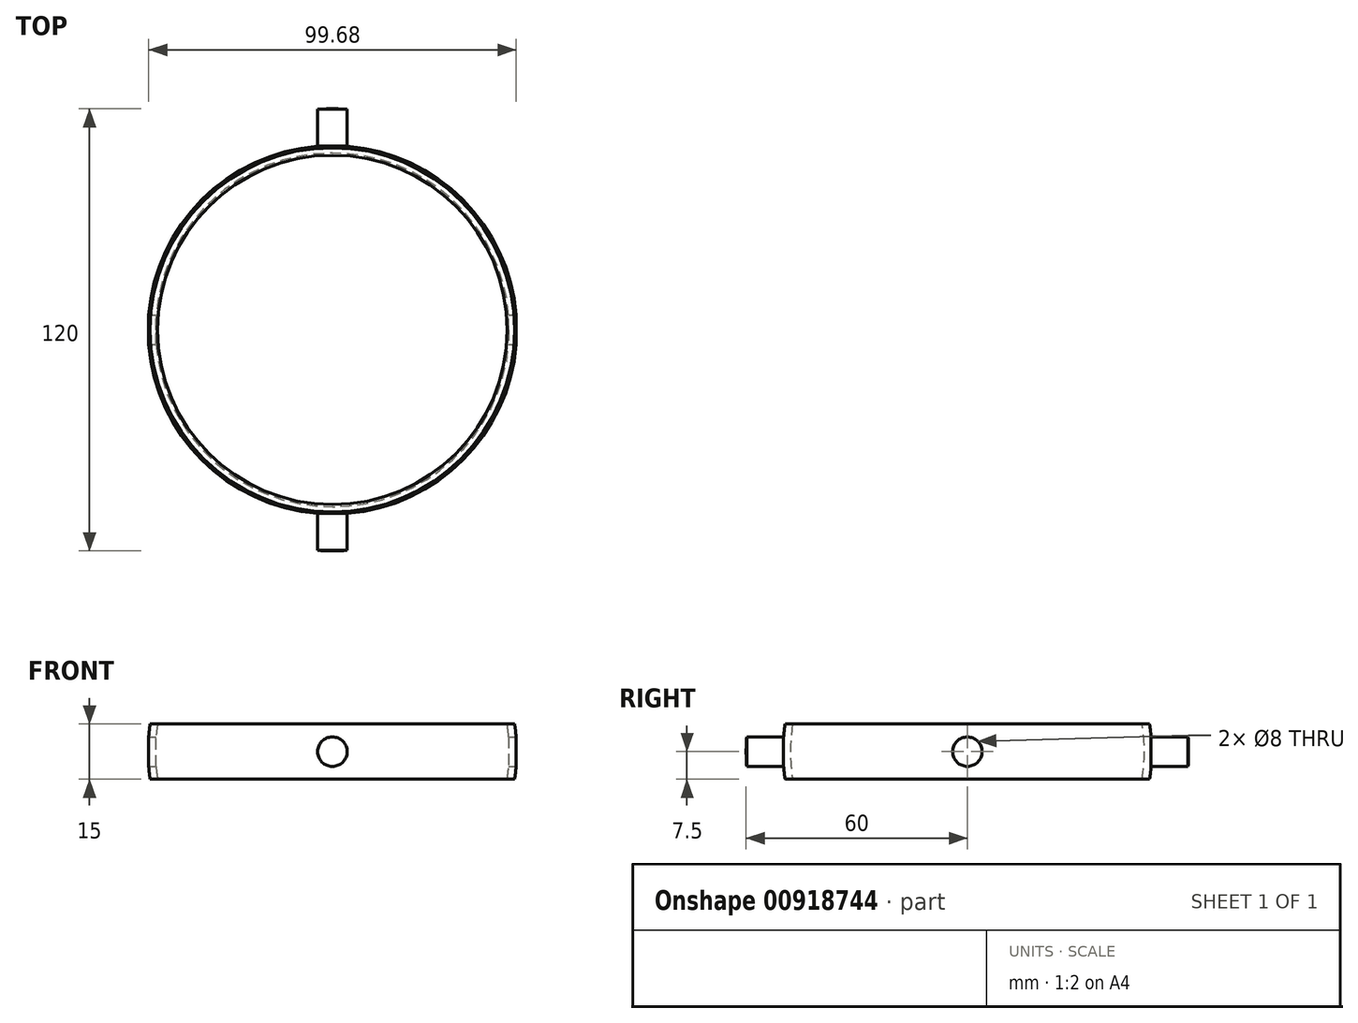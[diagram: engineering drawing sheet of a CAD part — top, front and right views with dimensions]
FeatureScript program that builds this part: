
annotation { "Feature Type Name" : "Feature", "Feature Type Description" : "" }
export const myFeature = defineFeature(function(context is Context, id is Id, definition is map)
    precondition{}
    {
        {
            var Q0;
            Q0=qCreatedBy(makeId("Front.planeOp"),FACE);
            var sketch = newSketch(context, id + "F0", { "sketchPlane" : qUnion([Q0])});
            skLineSegment(sketch, "E0", {"start": v(0, 15) * mm, "end": v(0, 0) * mm});
            skLineSegment(sketch, "E1", {"start": v(0, 0) * mm, "end": v(-54.5, 0) * mm});
            skArc(sketch, "E2", {"start": v(-49.43, 7.5) * mm, "mid": v(-50, 0) * mm, "end": v(-49.43, -7.5) * mm});
            skPoint(sketch, "E2.startSnap0", {"position": v(0, 7.5) * mm});
            skArc(sketch, "E3", {"start": v(-47.41, 7.5) * mm, "mid": v(-48, 0) * mm, "end": v(-47.41, -7.5) * mm});
            skLineSegment(sketch, "E4", {"start": v(-49.43, 7.5) * mm, "end": v(-47.41, 7.5) * mm});
            skLineSegment(sketch, "E5", {"start": v(-49.43, -7.5) * mm, "end": v(-47.41, -7.5) * mm});
            skSolve(sketch);
        }
        {
            var Q0;
            Q0 = qSketchRegion(id + "F0", true);
            var Q1;
            Q1=sQuery(id+"F0.wireOp",EDGE,"E0");
            revolve(context, id + "F1", {"surfaceOperationType" : NewSurfaceOperationType.NEW, "entities" : qUnion([Q0]), "axis" : qUnion([Q1]), "revolveType" : RevolveType.FULL});
        }
        {
            var Q0;
            Q0=qCreatedBy(makeId("Right.planeOp"),FACE);
            var sketch = newSketch(context, id + "F2", { "sketchPlane" : qUnion([Q0])});
            skCircle(sketch, "E6", {"center": v(0, 0) * mm, "radius": 4 * mm});
            skLineSegment(sketch, "E7", {"start": v(0, 7.5) * mm, "end": v(0, 0) * mm});
            skSolve(sketch);
        }
        {
            var Q0;
            Q0 = qSketchRegion(id + "F2", true);
            extrude(context, id + "F3", {"entities" : qUnion([Q0]), "operationType" : NewBodyOperationType.REMOVE, "endBound" : BoundingType.THROUGH_ALL, "oppositeDirection" : true, "depth" : 25.4 * mm, "offsetDistance" : 25.4 * mm, "hasSecondDirection" : true, "secondDirectionBound" : SecondDirectionBoundingType.THROUGH_ALL, "secondDirectionOppositeDirection" : false, "secondDirectionDepth" : 25.4 * mm});
        }
        {
            var Q0;
            Q0=qCreatedBy(makeId("Front.planeOp"),FACE);
            cPlane(context, id + "F4", {"entities" : qUnion([Q0]), "cplaneType" : CPlaneType.OFFSET, "offset" : 60 * mm, "width" : 152.4 * mm, "height" : 152.4 * mm});
        }
        {
            var Q0;
            Q0=qCreatedBy(id+"F4.planeOp",FACE);
            var sketch = newSketch(context, id + "F5", { "sketchPlane" : qUnion([Q0])});
            skCircle(sketch, "E8", {"center": v(0, 0) * mm, "radius": 4 * mm});
            skSolve(sketch);
        }
        {
            var Q0;
            Q0=makeQuery(id+"F5.imprint","IMPRINT",FACE,{"disambiguationData":[TD([[makeQuery(id+"F5.imprint","IMPRINT",EDGE,{"derivedFrom":sQuery(id+"F5.wireOp",EDGE,"E8")}),1.0]])]});
            var Q1;
            Q1=sQuery(id+"F5.wireOp",EDGE,"E8");
            var Q2;
            Q2=makeQuery(id+"F1.opRevolve","SWEPT_FACE",FACE,{"disambiguationData":[OSD([sQuery(id+"F0.wireOp",EDGE,"E2")])]});
            extrude(context, id + "F6", {"entities" : qUnion([Q0]), "operationType" : NewBodyOperationType.ADD, "surfaceEntities" : qUnion([Q1]), "depth" : 0 * mm, "offsetDistance" : 25.4 * mm, "hasSecondDirection" : true, "secondDirectionBound" : SecondDirectionBoundingType.UP_TO_SURFACE, "secondDirectionOppositeDirection" : true, "secondDirectionDepth" : 25.4 * mm, "secondDirectionBoundEntityFace" : qUnion([Q2])});
        }
        {
            var Q0;
            Q0=makeQuery(id+"F1.opRevolve","SWEPT_BODY",BODY,{"disambiguationData":[OSD([sQuery(id+"F0.wireOp",EDGE,"E2"),sQuery(id+"F0.wireOp",EDGE,"E3"),sQuery(id+"F0.wireOp",EDGE,"E4"),sQuery(id+"F0.wireOp",EDGE,"E5")])]});
            var Q1;
            Q1=qCreatedBy(makeId("Front.planeOp"),FACE);
            mirror(context, id + "F7", {"operationType" : NewBodyOperationType.ADD, "entities" : qUnion([Q0]), "mirrorPlane" : qUnion([Q1])});
        }
        {
            var Q0;
            Q0=qCreatedBy(makeId("Right.planeOp"),FACE);
            var sketch = newSketch(context, id + "F8", { "sketchPlane" : qUnion([Q0])});
            skLineSegment(sketch, "E9", {"start": v(0, 70) * mm, "end": v(0, 0) * mm});
            skLineSegment(sketch, "E10", {"start": v(0, 0) * mm, "end": v(-50.63, 0) * mm});
            skArc(sketch, "E11", {"start": v(0, 70) * mm, "mid": v(-70, 0) * mm, "end": v(0, -70) * mm});
            skArc(sketch, "E12", {"start": v(0, 60) * mm, "mid": v(-60, 0) * mm, "end": v(0, -60) * mm});
            skLineSegment(sketch, "E13", {"start": v(0, -60) * mm, "end": v(0, -70) * mm});
            skSolve(sketch);
        }
        {
            var Q0;
            Q0 = qSketchRegion(id + "F8", true);
            var Q1;
            Q1=sQuery(id+"F8.wireOp",EDGE,"E9");
            revolve(context, id + "F9", {"operationType" : NewBodyOperationType.REMOVE, "surfaceOperationType" : NewSurfaceOperationType.NEW, "entities" : qUnion([Q0]), "axis" : qUnion([Q1]), "revolveType" : RevolveType.FULL, "oppositeDirection" : true});
        }
    });
